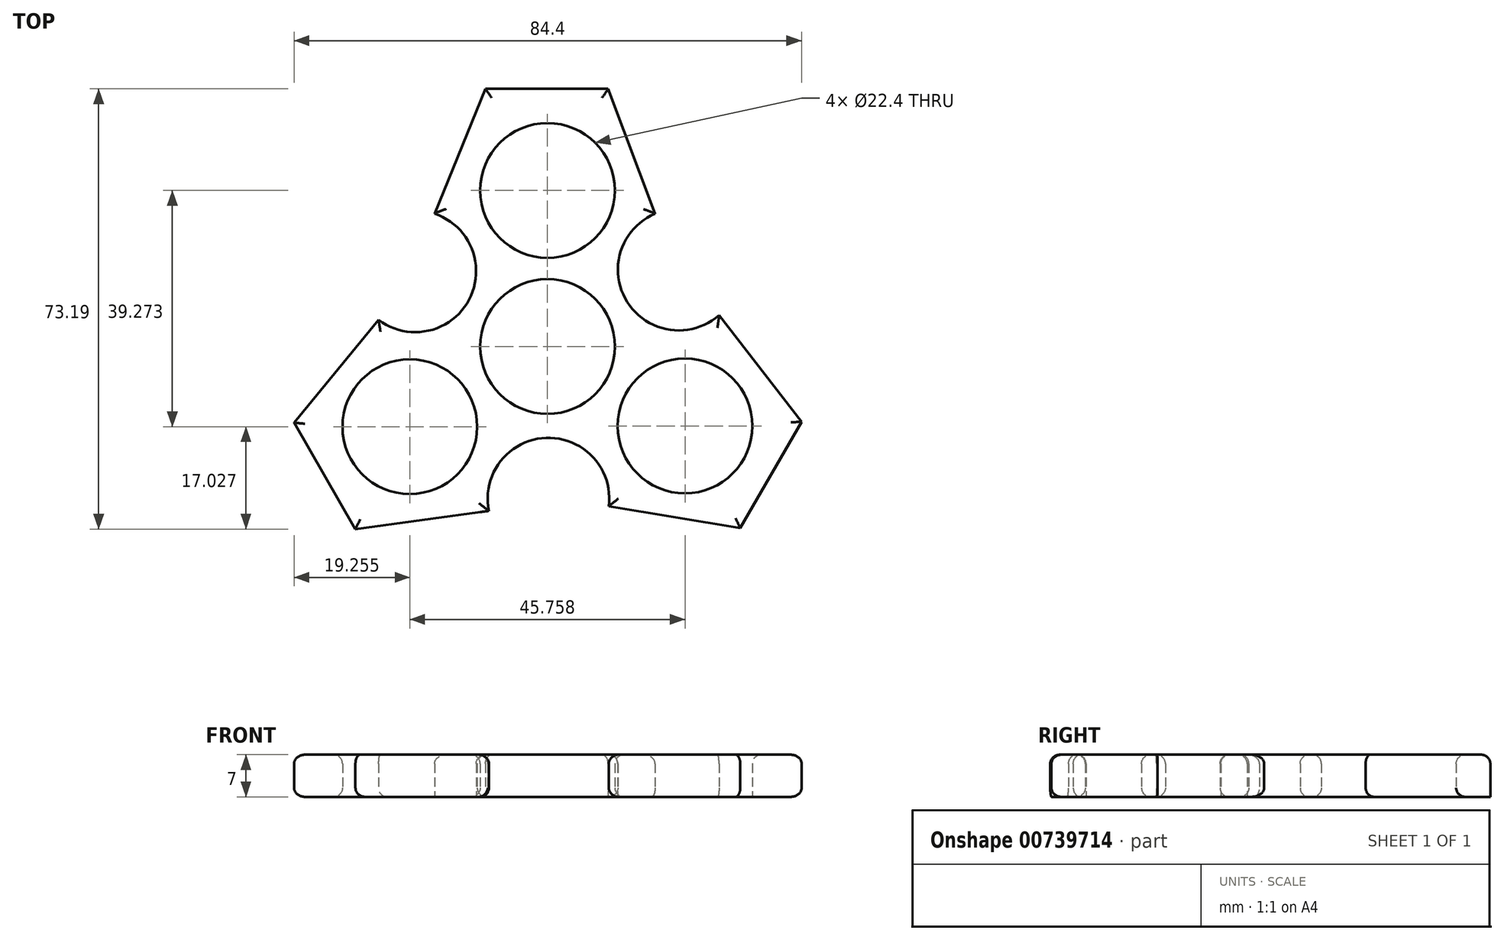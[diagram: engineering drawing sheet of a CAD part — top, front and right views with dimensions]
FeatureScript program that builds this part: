
annotation { "Feature Type Name" : "Feature", "Feature Type Description" : "" }
export const myFeature = defineFeature(function(context is Context, id is Id, definition is map)
    precondition{}
    {
        {
            var Q0;
            Q0=qCreatedBy(makeId("Top.planeOp"),FACE);
            var sketch = newSketch(context, id + "F0", { "sketchPlane" : qUnion([Q0])});
            skCircle(sketch, "E0", {"center": v(0, 0) * mm, "radius": 11.2 * mm});
            skCircle(sketch, "E1", {"center": v(0, 25.95) * mm, "radius": 11.2 * mm});
            skCircle(sketch, "E2", {"center": v(-22.9, -13.32) * mm, "radius": 11.2 * mm});
            skCircle(sketch, "E3", {"center": v(22.86, -13.2) * mm, "radius": 11.2 * mm});
            skLineSegment(sketch, "E4", {"start": v(-10.31, 42.84) * mm, "end": v(10.1, 42.84) * mm});
            skLineSegment(sketch, "E5", {"start": v(-10.31, 42.84) * mm, "end": v(-18.79, 22.1) * mm});
            skLineSegment(sketch, "E6", {"start": v(10.1, 42.84) * mm, "end": v(17.88, 22.1) * mm});
            skLineSegment(sketch, "E7.1.0", {"start": v(-31.94, -30.35) * mm, "end": v(-42.15, -12.68) * mm});
            skLineSegment(sketch, "E7.1.1", {"start": v(-31.94, -30.35) * mm, "end": v(-9.74, -27.32) * mm});
            skLineSegment(sketch, "E7.1.2", {"start": v(-42.15, -12.68) * mm, "end": v(-28.07, 4.44) * mm});
            skLineSegment(sketch, "E7.2.0", {"start": v(42.25, -12.49) * mm, "end": v(32.05, -30.16) * mm});
            skLineSegment(sketch, "E7.2.1", {"start": v(42.25, -12.49) * mm, "end": v(28.53, 5.22) * mm});
            skLineSegment(sketch, "E7.2.2", {"start": v(32.05, -30.16) * mm, "end": v(10.2, -26.53) * mm});
            skArc(sketch, "E8", {"start": v(-28.07, 4.44) * mm, "mid": v(-13.03, 7.8) * mm, "end": v(-18.79, 22.1) * mm});
            skArc(sketch, "E9.1.0", {"start": v(10.2, -26.53) * mm, "mid": v(-0.23, -15.18) * mm, "end": v(-9.74, -27.32) * mm});
            skArc(sketch, "E9.2.0", {"start": v(17.88, 22.1) * mm, "mid": v(13.27, 7.39) * mm, "end": v(28.53, 5.22) * mm});
            skSolve(sketch);
        }
        {
            var Q0;
            Q0=makeQuery(id+"F0.imprint","IMPRINT",FACE,{"disambiguationData":[TD([[makeQuery(id+"F0.imprint","IMPRINT",EDGE,{"derivedFrom":sQuery(id+"F0.wireOp",EDGE,"E0")}),-1.0]])]});
            extrude(context, id + "F1", {"entities" : qUnion([Q0]), "depth" : 7 * mm, "offsetDistance" : 25 * mm});
        }
        {
            var Q0;
            Q0=makeQuery(id+"F1.opExtrude","CAP_EDGE",EDGE,{"disambiguationData":[OSD([sQuery(id+"F0.wireOp",EDGE,"E5")])],"isStart":false});
            var Q1;
            Q1=makeQuery(id+"F1.opExtrude","CAP_EDGE",EDGE,{"disambiguationData":[OSD([sQuery(id+"F0.wireOp",EDGE,"E4")])],"isStart":false});
            var Q2;
            Q2=makeQuery(id+"F1.opExtrude","CAP_EDGE",EDGE,{"disambiguationData":[OSD([sQuery(id+"F0.wireOp",EDGE,"E6")])],"isStart":false});
            var Q3;
            Q3=makeQuery(id+"F1.opExtrude","CAP_EDGE",EDGE,{"disambiguationData":[OSD([sQuery(id+"F0.wireOp",EDGE,"E9.2.0")])],"isStart":false});
            var Q4;
            Q4=makeQuery(id+"F1.opExtrude","CAP_EDGE",EDGE,{"disambiguationData":[OSD([sQuery(id+"F0.wireOp",EDGE,"E7.1.2")])],"isStart":false});
            var Q5;
            Q5=makeQuery(id+"F1.opExtrude","CAP_EDGE",EDGE,{"disambiguationData":[OSD([sQuery(id+"F0.wireOp",EDGE,"E7.1.0")])],"isStart":false});
            var Q6;
            Q6=makeQuery(id+"F1.opExtrude","CAP_FACE",FACE,{"disambiguationData":[OSD([sQuery(id+"F0.wireOp",EDGE,"E0"),sQuery(id+"F0.wireOp",EDGE,"E1"),sQuery(id+"F0.wireOp",EDGE,"E2"),sQuery(id+"F0.wireOp",EDGE,"E3"),sQuery(id+"F0.wireOp",EDGE,"E4"),sQuery(id+"F0.wireOp",EDGE,"E5"),sQuery(id+"F0.wireOp",EDGE,"E6"),sQuery(id+"F0.wireOp",EDGE,"E7.1.0"),sQuery(id+"F0.wireOp",EDGE,"E7.1.1"),sQuery(id+"F0.wireOp",EDGE,"E7.1.2"),sQuery(id+"F0.wireOp",EDGE,"E7.2.0"),sQuery(id+"F0.wireOp",EDGE,"E7.2.1"),sQuery(id+"F0.wireOp",EDGE,"E7.2.2"),sQuery(id+"F0.wireOp",EDGE,"E8"),sQuery(id+"F0.wireOp",EDGE,"E9.1.0"),sQuery(id+"F0.wireOp",EDGE,"E9.2.0")])],"isStart":false});
            var Q7;
            Q7=makeQuery(id+"F1.opExtrude","CAP_EDGE",EDGE,{"disambiguationData":[OSD([sQuery(id+"F0.wireOp",EDGE,"E9.1.0")])],"isStart":true});
            var Q8;
            Q8=makeQuery(id+"F1.opExtrude","CAP_EDGE",EDGE,{"disambiguationData":[OSD([sQuery(id+"F0.wireOp",EDGE,"E7.1.0")])],"isStart":true});
            var Q9;
            Q9=makeQuery(id+"F1.opExtrude","CAP_EDGE",EDGE,{"disambiguationData":[OSD([sQuery(id+"F0.wireOp",EDGE,"E2")])],"isStart":true});
            var Q10;
            Q10=makeQuery(id+"F1.opExtrude","CAP_EDGE",EDGE,{"disambiguationData":[OSD([sQuery(id+"F0.wireOp",EDGE,"E7.1.2")])],"isStart":true});
            var Q11;
            Q11=makeQuery(id+"F1.opExtrude","CAP_EDGE",EDGE,{"disambiguationData":[OSD([sQuery(id+"F0.wireOp",EDGE,"E1")])],"isStart":true});
            var Q12;
            Q12=makeQuery(id+"F1.opExtrude","CAP_EDGE",EDGE,{"disambiguationData":[OSD([sQuery(id+"F0.wireOp",EDGE,"E0")])],"isStart":true});
            var Q13;
            Q13=makeQuery(id+"F1.opExtrude","CAP_EDGE",EDGE,{"disambiguationData":[OSD([sQuery(id+"F0.wireOp",EDGE,"E7.2.2")])],"isStart":true});
            var Q14;
            Q14=makeQuery(id+"F1.opExtrude","CAP_EDGE",EDGE,{"disambiguationData":[OSD([sQuery(id+"F0.wireOp",EDGE,"E7.2.0")])],"isStart":true});
            var Q15;
            Q15=makeQuery(id+"F1.opExtrude","CAP_EDGE",EDGE,{"disambiguationData":[OSD([sQuery(id+"F0.wireOp",EDGE,"E7.2.1")])],"isStart":true});
            var Q16;
            Q16=makeQuery(id+"F1.opExtrude","CAP_EDGE",EDGE,{"disambiguationData":[OSD([sQuery(id+"F0.wireOp",EDGE,"E9.2.0")])],"isStart":true});
            fillet(context, id + "F2", {"entities" : qUnion([Q0, Q1, Q2, Q3, Q4, Q5, Q6, Q7, Q8, Q9, Q10, Q11, Q12, Q13, Q14, Q15, Q16]), "radius" : 1.5 * mm, "tangentPropagation" : true, "allowEdgeOverflow" : false});
        }
    });
